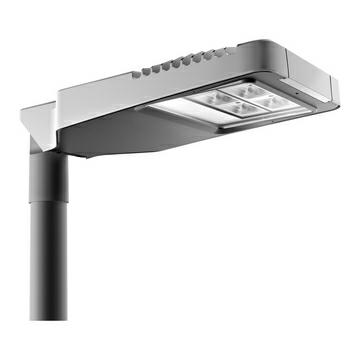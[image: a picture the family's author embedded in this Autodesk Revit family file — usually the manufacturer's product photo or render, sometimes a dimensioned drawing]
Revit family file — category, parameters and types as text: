
# Revit family: Lighting-StreetLighting-GEWISS-ROAD[5]MEDIUM-LED_OPTIC_HUGE_CLI
name_source: partatom
category: Apparecchi per illuminazione
units: mm (PartAtom-declared; Revit-internal decimal feet)

## family parameters
Basato su piano di lavoro = No
Condiviso = No
Punto di calcolo locali = No
Quota connettore circolare = Usa diametro
Sempre verticale = Sì
Sorgente d'illuminazione = No
Taglio con vuoti quando caricato = No
Tipo di parte = Normale

## types (48) — shared parameters
Applicazione = External
Catalogue = LIGHTING
Catalogue Range = ROAD [5]
Electrocod = 244C
IDF = adde9699-6c35-4d07-bf14-12043a13b976
IDT = 9a00d1bcfceb457b92ad59b7f4a86d78
IP degree = IP66
Immagine tipo = GWR5276M.jpg
Insulation class = I
Lamp- = LED
Lampada = LED
Maximum surface exposed to the wind = 0,19M2
Minimum distance from the illuminated object = 1M
Produttore = GEWISS S.p.A.
SEO = Street lighting
Shock resistance = IK08
Technical sheet = https://www.gewiss.com
Tilt adjustable = -20° ÷ +10° side bracket - -10° ÷ +20° pole head
Tipo alimentatore = Constant Current Driver Led
URL = https://www.gewiss.com
Version file RFA = 20.11
Warranty = 5 years

## per-type parameters (varying)
- GWR5616M - ROAD5 MEDI HUGE 6M 4000K 0,85A CL1 1-10V: Colour temperature=4000 K (CRI 70); Colour temperature:=4000 K (CRI 70); Descrizione=ROAD5 MEDI HUGE 6M 4000K 0,85A CL1 1-10V; EAN code=8011564874404; LED LifeTime (L80B05)=120000H; LED current.=0,85A; Lumen output (lm)=17160; Modello=GWR5616M; No. Chorus modules=6 (6x3 LED); Nominal flux (lm)=24330; Number of modules=6 (6x3 LED); Operating temperature:=-25 +40 °C; Optic=H - ULOR: 0%; Overvoltage resistance=12 KV (Common and dfferential mode); Pilot current=0,85A; Power supply operation=Dimmable; System power=185W; Tipologia=Dimmable; Voltage-=220/240 V - 50/60 Hz - Dimmable 1-10 V; Weight (kg)=9.1; Weight (kg):=9,1; Working temperature=-25 +40 °C
- GWR5616B - ROAD5 MEDI HUGE 6M 4000K 0,85A CL1 BIREG: Colour temperature=4000 K (CRI 70); Colour temperature:=4000 K (CRI 70); Descrizione=ROAD5 MED. HUGE 6M 4000K 0,85A CL1 BI-PO; EAN code=8011564874398; LED LifeTime (L80B05)=120000H; LED current.=0,85A; Lumen output (lm)=17160; Modello=GWR5616B; No. Chorus modules=6 (6x3 LED); Nominal flux (lm)=24330; Number of modules=6 (6x3 LED); Operating temperature:=-25 +40 °C; Optic=H - ULOR: 0%; Overvoltage resistance=12 KV (Common and dfferential mode); Pilot current=0,85A; Power supply operation=Bi power; System power=187W; Tipologia=Bi power; Voltage-=220/240 V - 50/60 Hz - Bi-power with self-learning; Weight (kg)=9.1; Weight (kg):=9,1; Working temperature=-25 +40 °C
- GWR5674B30K - ROAD5 MEDI HUGE 4M 3000K 0,7A CL1 BIREG: Body=Die-cast aluminium -; Classification:=-; Color Rendering Index=CRI-70; Colore=Graphite grey; Colour :=Powder coating; Colour temperature=3000K; Colour temperature:=3000 K (CRI>80); Context=Street and parking lighting; Control System=Bi-power with self-learning; DIN 18032-3 certification=-; Descrizione=GWR5674B30K - ROAD5 MEDI HUGE 4M 3000K 0,7A CL1 BIREG; Device with reduced surface temperature=-; Driver=Included; Driver Box=Built-in; Efficiency (lm/W)=96; Eletrical and lighting features=-; External screw=Stainless steel; Fixing=Pole Head - Outreach; Gasket=Anti-aging silicone; General information=-; Glow Wire Test :=-; IPEA=ROAD = A // LARGE AREAS = A ++ // CYCLOPEDONALS = A // GREEN AREAS = A // HISTORICAL CENTER = A3 +; Installationa and maintenance=-; LED Life Time (L80B05)=77000H; LED Maintenance=Not available; LED current.=0,7A; Lifetime=L90B10 (Tq+25°C) = 100.000 h - L90B10 (Tq+50°C) = 50.000 h; Locking Hook=Integrated front handle; Lumen output (lm)=10400; Luminaire=LED Road Equipment; Materials=-; Maximum surface exposed to the wind :=0.19 m2; Modello=GWR5674B30K; Mouting and installation=Pole Head - Outreach; Nominal flux (lm)=10800; Number of modules=4 (4x3 LED); Operating temperature :=-25 +50 °C; Operating temperature:=-25 +50 °C; Optic=HUGE; Optic :=Metallized polycarbonate reflector; Optic Maintenance=Not available; Optic and illuminating features=-; Overvoltage protection=DM 10KV / CM 10KV; Overvoltage resistance :=Common and dfferential mode: 10KV; Photobiological Risk Class=RG0; Power supply operation=Bi power; Rated frequency (Hz)=50 / 60; Shield type=4mm thick flat tempered glass; Standard Deviation Colour Matching=SDCM = 5; Standard-=EN 60598-2-3, EN 60598-1 IEC/TR 62778; Standards and approvals=-; Stocking temperature=-; Supply voltage=220 - 240 V; System power=108W; System power :=108 W @ 0.7A; Tilt-=-20° ÷ +10° side bracket - -10° ÷ +20° pole head; Tipologia=Bi power; Type of light source=LED - Not replaceable; Unified Glare Rating=G*3 - ULOR = 0; Unique digital code (Datamatrix)=Currently not present; Voltage-=220/240 V - 50/60 Hz - Bi-power with self-learning; Weight (kg):=8,4; Wiring=Isolating switch
- GWR561330K - ROAD5 MEDI HUGE 3M 3000K 1,0A CL1: Body=Die-cast aluminium -; Classification:=-; Color Rendering Index=CRI-70; Colore=Graphite grey; Colour :=Powder coating; Colour temperature=3000K; Colour temperature:=3000 K (CRI>80); Context=Street and parking lighting; Control System=Stand alone; DIN 18032-3 certification=-; Descrizione=GWR561330K - ROAD5 MEDI HUGE 3M 3000K 1,0A CL1; Device with reduced surface temperature=-; Driver=Included; Driver Box=Built-in; Efficiency (lm/W)=93; Eletrical and lighting features=-; External screw=Stainless steel; Fixing=Pole Head - Outreach; Gasket=Anti-aging silicone; General information=-; Glow Wire Test :=-; IPEA=ROAD = A // LARGE AREAS = A ++ // CYCLOPEDONALS = B // GREEN AREAS = B // HISTORICAL CENTER = A3 +; Installationa and maintenance=-; LED Life Time (L80B05)=120000H; LED Maintenance=Not available; LED current.=1A; Lifetime=L90B10 (Tq+25°C) = 100.000 h - L90B10 (Tq+40°C) = 75.000 h; Locking Hook=Integrated front handle; Lumen output (lm)=10500; Luminaire=LED Road Equipment; Materials=-; Maximum surface exposed to the wind :=0.19 m2; Modello=GWR561330K; Mouting and installation=Pole Head - Outreach; Nominal flux (lm)=12420; Number of modules=3 (3x3 LED); Operating temperature :=-25 +40 °C; Operating temperature:=-25 +40 °C; Optic=HUGE; Optic :=Metallized polycarbonate reflector; Optic Maintenance=Not available; Optic and illuminating features=-; Overvoltage protection=DM 10KV / CM 10KV; Overvoltage resistance :=Common and dfferential mode: 10KV; Photobiological Risk Class=RG0; Rated frequency (Hz)=50 / 60; Shield type=4mm thick flat tempered glass; Standard Deviation Colour Matching=SDCM = 5; Standard-=EN 60598-2-3, EN 60598-1 IEC/TR 62778; Standards and approvals=-; Stocking temperature=-; Supply voltage=220 - 240 V; System power=113W; System power :=113 W @ 1A; Tilt-=-20° ÷ +10° side bracket - -10° ÷ +20° pole head; Tipologia=Stand alone; Type of light source=LED - Not replaceable; Unified Glare Rating=G*3 - ULOR = 0; Unique digital code (Datamatrix)=Currently not present; Voltage-=220/240 V - 50/60 Hz - Stand alone; Weight (kg):=8; Wiring=Isolating switch
- GWR5616B30K - ROAD5 MEDI HUGE 6M 3000K 0,85A CL1 BIREG: Body=Die-cast aluminium -; Classification:=-; Color Rendering Index=CRI-70; Colore=Graphite grey; Colour :=Powder coating; Colour temperature=3000K; Colour temperature:=3000 K (CRI>80); Context=Street and parking lighting; Control System=Bi-power with self-learning; DIN 18032-3 certification=-; Descrizione=GWR5616B30K - ROAD5 MEDI HUGE 6M 3000K 0,85A CL1 BIREG; Device with reduced surface temperature=-; Driver=Included; Driver Box=Built-in; Efficiency (lm/W)=98; Eletrical and lighting features=-; External screw=Stainless steel; Fixing=Pole Head - Outreach; Gasket=Anti-aging silicone; General information=-; Glow Wire Test :=-; IPEA=ROAD = B // LARGE AREAS = A ++ // CYCLOPEDONALS = B // GREEN AREAS = B // HISTORICAL CENTER = A3 +; Installationa and maintenance=-; LED Life Time (L80B05)=120000H; LED Maintenance=Not available; LED current.=0,849999999999999A; Lifetime=L90B10 (Tq+25°C) = 100.000 h - L90B10 (Tq+40°C) = 50.000 h; Locking Hook=Integrated front handle; Lumen output (lm)=18400; Luminaire=LED Road Equipment; Materials=-; Maximum surface exposed to the wind :=0.19 m2; Modello=GWR5616B30K; Mouting and installation=Pole Head - Outreach; Nominal flux (lm)=21114; Number of modules=6 (6x3 LED); Operating temperature :=-25 +40 °C; Operating temperature:=-25 +40 °C; Optic=HUGE; Optic :=Metallized polycarbonate reflector; Optic Maintenance=Not available; Optic and illuminating features=-; Overvoltage protection=DM 10KV / CM 10KV; Overvoltage resistance :=Common and dfferential mode: 10KV; Photobiological Risk Class=RG0; Power supply operation=Bi power; Rated frequency (Hz)=50 / 60; Shield type=4mm thick flat tempered glass; Standard Deviation Colour Matching=SDCM = 5; Standard-=EN 60598-2-3, EN 60598-1 IEC/TR 62778; Standards and approvals=-; Stocking temperature=-; Supply voltage=220 - 240 V; System power=187W; System power :=187 W @ 0.85A; Tilt-=-20° ÷ +10° side bracket - -10° ÷ +20° pole head; Tipologia=Bi power; Type of light source=LED - Not replaceable; Unified Glare Rating=G*3 - ULOR = 0; Unique digital code (Datamatrix)=Currently not present; Voltage-=220/240 V - 50/60 Hz - Bi-power with self-learning; Weight (kg):=9,09999999999999; Wiring=Isolating switch
- GWR5674M - ROAD5 MEDI HUGE 4M 4000K 0,7A CL1 1-10V: Colour temperature=4000 K (CRI 70); Colour temperature:=4000 K (CRI 70); Descrizione=ROAD5 MEDI HUGE 4M 4000K 0,7A CL1 1-10V; EAN code=8011564874534; LED LifeTime (L80B05)=77000H; LED current.=0,7A; Lumen output (lm)=9190; Modello=GWR5674M; No. Chorus modules=4 (4x3 LED); Nominal flux (lm)=12480; Number of modules=4 (4x3 LED); Operating temperature:=-25 +50 °C; Optic=H - ULOR: 0%; Overvoltage resistance=12 KV (Common and dfferential mode); Pilot current=0,7A; Power supply operation=Dimmable; System power=106W; Tipologia=Dimmable; Voltage-=220/240 V - 50/60 Hz - Dimmable 1-10 V; Weight (kg)=8,4; Weight (kg):=8,4; Working temperature=-25 +50 °C
- GWR5614 - ROAD5 MEDI HUGE 4M 4000K 1,0A CL1: Colour temperature=4000 K (CRI 70); Colour temperature:=4000 K (CRI 70); Descrizione=ROAD5 MEDI HUGE 4M 4000K 1,0A CL1; EAN code=8011564874329; LED LifeTime (L80B05)=120000H; LED current.=1A; Lumen output (lm)=13460; Modello=GWR5614; No. Chorus modules=4 (4x3 LED); Nominal flux (lm)=19080; Number of modules=4 (4x3 LED); Operating temperature:=-25 +40 °C; Optic=H - ULOR: 0%; Overvoltage resistance=12 KV (Common and dfferential mode); Pilot current=1A; System power=151W; Tipologia=Stand alone; Voltage-=220/240 V - 50/60 Hz - Stand alone; Weight (kg)=8,4; Weight (kg):=8,4; Working temperature=-25 +40 °C
- GWR5673M - ROAD5 MEDI HUGE 3M 4000K 0,7A CL1 1-10V: Colour temperature=4000 K (CRI 70); Colour temperature:=4000 K (CRI 70); Descrizione=ROAD5 MEDI HUGE 3M 4000K 0,7A CL1 1-10V; EAN code=8011564874503; LED LifeTime (L80B05)=77000H; LED current.=0,7A; Lumen output (lm)=6890; Modello=GWR5673M; No. Chorus modules=3 (3x3 LED); Nominal flux (lm)=9360; Number of modules=3 (3x3 LED); Operating temperature:=-25 +50 °C; Optic=H - ULOR: 0%; Overvoltage resistance=12 KV (Common and dfferential mode); Pilot current=0,7A; Power supply operation=Dimmable; System power=79W; Tipologia=Dimmable; Voltage-=220/240 V - 50/60 Hz - Dimmable 1-10 V; Weight (kg)=8; Weight (kg):=8; Working temperature=-25 +50 °C
- GWR5676M30K - ROAD5 MEDI HUGE 6M 3000K 0,7A CL1 1-10V: Body=Die-cast aluminium -; Classification:=-; Color Rendering Index=CRI-70; Colore=Graphite grey; Colour :=Powder coating; Colour temperature=3000K; Colour temperature:=3000 K (CRI>80); Context=Street and parking lighting; Control System=Dimmable 1-10 V; DIN 18032-3 certification=-; Descrizione=GWR5676M30K - ROAD5 MEDI HUGE 6M 3000K 0,7A CL1 1-10V; Device with reduced surface temperature=-; Driver=Included; Driver Box=Built-in; Efficiency (lm/W)=97; Eletrical and lighting features=-; External screw=Stainless steel; Fixing=Pole Head - Outreach; Gasket=Anti-aging silicone; General information=-; Glow Wire Test :=-; IPEA=ROAD = B // LARGE AREAS = A ++ // CYCLOPEDONALS = A // GREEN AREAS = A // HISTORICAL CENTER = A3 +; Installationa and maintenance=-; LED Life Time (L80B05)=77000H; LED Maintenance=Not available; LED current.=0,7A; Lifetime=L90B10 (Tq+25°C) = 100.000 h - L90B10 (Tq+50°C) = 50.000 h; Locking Hook=Integrated front handle; Lumen output (lm)=15600; Luminaire=LED Road Equipment; Materials=-; Maximum surface exposed to the wind :=0.19 m2; Modello=GWR5676M30K; Mouting and installation=Pole Head - Outreach; Nominal flux (lm)=16200; Number of modules=6 (6x3 LED); Operating temperature :=-25 +50 °C; Operating temperature:=-25 +50 °C; Optic=HUGE; Optic :=Metallized polycarbonate reflector; Optic Maintenance=Not available; Optic and illuminating features=-; Overvoltage protection=DM 10KV / CM 10KV; Overvoltage resistance :=Common and dfferential mode: 10KV; Photobiological Risk Class=RG0; Power supply operation=Dimmable; Rated frequency (Hz)=50 / 60; Shield type=4mm thick flat tempered glass; Standard Deviation Colour Matching=SDCM = 5; Standard-=EN 60598-2-3, EN 60598-1 IEC/TR 62778; Standards and approvals=-; Stocking temperature=-; Supply voltage=220 - 240 V; System power=159W; System power :=161 W @ 0.7A; Tilt-=-20° ÷ +10° side bracket - -10° ÷ +20° pole head; Tipologia=Dimmable; Type of light source=LED - Not replaceable; Unified Glare Rating=G*3 - ULOR = 0; Unique digital code (Datamatrix)=Currently not present; Voltage-=220/240 V - 50/60 Hz - Dimmable 1-10 V; Weight (kg):=9,09999999999999; Wiring=Isolating switch
- GWR5675 - ROAD5 MEDI HUGE 5M 4000K 0,7A CL1: Colour temperature=4000 K (CRI 70); Colour temperature:=4000 K (CRI 70); Descrizione=ROAD5 MEDI HUGE 5M 4000K 0,7A CL1; EAN code=8011564874541; LED LifeTime (L80B05)=77000H; LED current.=0,7A; Lumen output (lm)=11480; Modello=GWR5675; No. Chorus modules=5 (5x3 LED); Nominal flux (lm)=15600; Number of modules=5 (5x3 LED); Operating temperature:=-25 +50 °C; Optic=H - ULOR: 0%; Overvoltage resistance=12 KV (Common and dfferential mode); Pilot current=0,7A; System power=132W; Tipologia=Stand alone; Voltage-=220/240 V - 50/60 Hz - Stand alone; Weight (kg)=8,8; Weight (kg):=8,8; Working temperature=-25 +50 °C
- GWR5675M - ROAD5 MEDI HUGE 5M 4000K 0,7A CL1 1-10V: Colour temperature=4000 K (CRI 70); Colour temperature:=4000 K (CRI 70); Descrizione=ROAD5 MEDI HUGE 5M 4000K 0,7A CL1 1-10V; EAN code=8011564874565; LED LifeTime (L80B05)=77000H; LED current.=0,7A; Lumen output (lm)=11480; Modello=GWR5675M; No. Chorus modules=5 (5x3 LED); Nominal flux (lm)=15600; Number of modules=5 (5x3 LED); Operating temperature:=-25 +50 °C; Optic=H - ULOR: 0%; Overvoltage resistance=12 KV (Common and dfferential mode); Pilot current=0,7A; Power supply operation=Dimmable; System power=132W; Tipologia=Dimmable; Voltage-=220/240 V - 50/60 Hz - Dimmable 1-10 V; Weight (kg)=8,8; Weight (kg):=8,8; Working temperature=-25 +50 °C
- GWR567430K - ROAD5 MEDI HUGE 4M 3000K 0,7A CL1: Body=Die-cast aluminium -; Classification:=-; Color Rendering Index=CRI-70; Colore=Graphite grey; Colour :=Powder coating; Colour temperature=3000K; Colour temperature:=3000 K (CRI>80); Context=Street and parking lighting; Control System=Stand alone; DIN 18032-3 certification=-; Descrizione=GWR567430K - ROAD5 MEDI HUGE 4M 3000K 0,7A CL1; Device with reduced surface temperature=-; Driver=Included; Driver Box=Built-in; Efficiency (lm/W)=98; Eletrical and lighting features=-; External screw=Stainless steel; Fixing=Pole Head - Outreach; Gasket=Anti-aging silicone; General information=-; Glow Wire Test :=-; IPEA=ROAD = A // LARGE AREAS = A3 + // CYCLOPEDONALS = A // GREEN AREAS = A // HISTORICAL CENTER = A4 +; Installationa and maintenance=-; LED Life Time (L80B05)=77000H; LED Maintenance=Not available; LED current.=0,7A; Lifetime=L90B10 (Tq+25°C) = 100.000 h - L90B10 (Tq+50°C) = 50.000 h; Locking Hook=Integrated front handle; Lumen output (lm)=10400; Luminaire=LED Road Equipment; Materials=-; Maximum surface exposed to the wind :=0.19 m2; Modello=GWR567430K; Mouting and installation=Pole Head - Outreach; Nominal flux (lm)=10800; Number of modules=4 (4x3 LED); Operating temperature :=-25 +50 °C; Operating temperature:=-25 +50 °C; Optic=HUGE; Optic :=Metallized polycarbonate reflector; Optic Maintenance=Not available; Optic and illuminating features=-; Overvoltage protection=DM 10KV / CM 10KV; Overvoltage resistance :=Common and dfferential mode: 10KV; Photobiological Risk Class=RG0; Rated frequency (Hz)=50 / 60; Shield type=4mm thick flat tempered glass; Standard Deviation Colour Matching=SDCM = 5; Standard-=EN 60598-2-3, EN 60598-1 IEC/TR 62778; Standards and approvals=-; Stocking temperature=-; Supply voltage=220 - 240 V; System power=106W; System power :=106 W @ 0.7A; Tilt-=-20° ÷ +10° side bracket - -10° ÷ +20° pole head; Tipologia=Stand alone; Type of light source=LED - Not replaceable; Unified Glare Rating=G*3 - ULOR = 0; Unique digital code (Datamatrix)=Currently not present; Voltage-=220/240 V - 50/60 Hz - Stand alone; Weight (kg):=8,4; Wiring=Isolating switch
- GWR561630K - ROAD5 MEDI HUGE 6M 3000K 0,85A CL1: Body=Die-cast aluminium -; Classification:=-; Color Rendering Index=CRI-70; Colore=Graphite grey; Colour :=Powder coating; Colour temperature=3000K; Colour temperature:=3000 K (CRI>80); Context=Street and parking lighting; Control System=Stand alone; DIN 18032-3 certification=-; Descrizione=GWR561630K - ROAD5 MEDI HUGE 6M 3000K 0,85A CL1; Device with reduced surface temperature=-; Driver=Included; Driver Box=Built-in; Efficiency (lm/W)=99; Eletrical and lighting features=-; External screw=Stainless steel; Fixing=Pole Head - Outreach; Gasket=Anti-aging silicone; General information=-; Glow Wire Test :=-; IPEA=ROAD = B // LARGE AREAS = A ++ // CYCLOPEDONALS = A // GREEN AREAS = A // HISTORICAL CENTER = A3 +; Installationa and maintenance=-; LED Life Time (L80B05)=120000H; LED Maintenance=Not available; LED current.=0,849999999999999A; Lifetime=L90B10 (Tq+25°C) = 100.000 h - L90B10 (Tq+40°C) = 50.000 h; Locking Hook=Integrated front handle; Lumen output (lm)=18400; Luminaire=LED Road Equipment; Materials=-; Maximum surface exposed to the wind :=0.19 m2; Modello=GWR561630K; Mouting and installation=Pole Head - Outreach; Nominal flux (lm)=21114; Number of modules=6 (6x3 LED); Operating temperature :=-25 +40 °C; Operating temperature:=-25 +40 °C; Optic=HUGE; Optic :=Metallized polycarbonate reflector; Optic Maintenance=Not available; Optic and illuminating features=-; Overvoltage protection=DM 10KV / CM 10KV; Overvoltage resistance :=Common and dfferential mode: 10KV; Photobiological Risk Class=RG0; Rated frequency (Hz)=50 / 60; Shield type=4mm thick flat tempered glass; Standard Deviation Colour Matching=SDCM = 5; Standard-=EN 60598-2-3, EN 60598-1 IEC/TR 62778; Standards and approvals=-; Stocking temperature=-; Supply voltage=220 - 240 V; System power=185W; System power :=185 W @ 0.85A; Tilt-=-20° ÷ +10° side bracket - -10° ÷ +20° pole head; Tipologia=Stand alone; Type of light source=LED - Not replaceable; Unified Glare Rating=G*3 - ULOR = 0; Unique digital code (Datamatrix)=Currently not present; Voltage-=220/240 V - 50/60 Hz - Stand alone; Weight (kg):=9,09999999999999; Wiring=Isolating switch
- GWR567630K - ROAD5 MEDI HUGE 6M 3000K 0,7A CL1: Body=Die-cast aluminium -; Classification:=-; Color Rendering Index=CRI-70; Colore=Graphite grey; Colour :=Powder coating; Colour temperature=3000K; Colour temperature:=3000 K (CRI>80); Context=Street and parking lighting; Control System=Stand alone; DIN 18032-3 certification=-; Descrizione=GWR567630K - ROAD5 MEDI HUGE 6M 3000K 0,7A CL1; Device with reduced surface temperature=-; Driver=Included; Driver Box=Built-in; Efficiency (lm/W)=98; Eletrical and lighting features=-; External screw=Stainless steel; Fixing=Pole Head - Outreach; Gasket=Anti-aging silicone; General information=-; Glow Wire Test :=-; IPEA=ROAD = B // LARGE AREAS = A ++ // CYCLOPEDONALS = A // GREEN AREAS = A // HISTORICAL CENTER = A4 +; Installationa and maintenance=-; LED Life Time (L80B05)=77000H; LED Maintenance=Not available; LED current.=0,7A; Lifetime=L90B10 (Tq+25°C) = 100.000 h - L90B10 (Tq+50°C) = 50.000 h; Locking Hook=Integrated front handle; Lumen output (lm)=15600; Luminaire=LED Road Equipment; Materials=-; Maximum surface exposed to the wind :=0.19 m2; Modello=GWR567630K; Mouting and installation=Pole Head - Outreach; Nominal flux (lm)=16200; Number of modules=6 (6x3 LED); Operating temperature :=-25 +50 °C; Operating temperature:=-25 +50 °C; Optic=HUGE; Optic :=Metallized polycarbonate reflector; Optic Maintenance=Not available; Optic and illuminating features=-; Overvoltage protection=DM 10KV / CM 10KV; Overvoltage resistance :=Common and dfferential mode: 10KV; Photobiological Risk Class=RG0; Rated frequency (Hz)=50 / 60; Shield type=4mm thick flat tempered glass; Standard Deviation Colour Matching=SDCM = 5; Standard-=EN 60598-2-3, EN 60598-1 IEC/TR 62778; Standards and approvals=-; Stocking temperature=-; Supply voltage=220 - 240 V; System power=159W; System power :=159 W @ 0.7A; Tilt-=-20° ÷ +10° side bracket - -10° ÷ +20° pole head; Tipologia=Stand alone; Type of light source=LED - Not replaceable; Unified Glare Rating=G*3 - ULOR = 0; Unique digital code (Datamatrix)=Currently not present; Voltage-=220/240 V - 50/60 Hz - Stand alone; Weight (kg):=9,09999999999999; Wiring=Isolating switch
- GWR5676 - ROAD5 MEDI HUGE 6M 4000K 0,7A CL1: Colour temperature=4000 K (CRI 70); Colour temperature:=4000 K (CRI 70); Descrizione=ROAD5 MEDI HUGE 6M 4000K 0,7A CL1; EAN code=8011564874572; LED LifeTime (L80B05)=77000H; LED current.=0,7A; Lumen output (lm)=13780; Modello=GWR5676; No. Chorus modules=6 (6x3 LED); Nominal flux (lm)=18720; Number of modules=6 (6x3 LED); Operating temperature:=-25 +50 °C; Optic=H - ULOR: 0%; Overvoltage resistance=12 KV (Common and dfferential mode); Pilot current=0,7A; System power=159W; Tipologia=Stand alone; Voltage-=220/240 V - 50/60 Hz - Stand alone; Weight (kg)=9.1; Weight (kg):=9,1; Working temperature=-25 +50 °C
- GWR5613 - ROAD5 MEDI HUGE 3M 4000K 1,0A CL1: Colour temperature=4000 K (CRI 70); Colour temperature:=4000 K (CRI 70); Descrizione=ROAD5 MEDI HUGE 3M 4000K 1,0A CL1; EAN code=8011564874091; LED LifeTime (L80B05)=120000H; LED current.=1A; Lumen output (lm)=10100; Modello=GWR5613; No. Chorus modules=3 (3x3 LED); Nominal flux (lm)=14310; Number of modules=3 (3x3 LED); Operating temperature:=-25 +40 °C; Optic=H - ULOR: 0%; Overvoltage resistance=12 KV (Common and dfferential mode); Pilot current=1A; System power=113W; Tipologia=Stand alone; Voltage-=220/240 V - 50/60 Hz - Stand alone; Weight (kg)=8; Weight (kg):=8; Working temperature=-25 +40 °C
- GWR5674M30K - ROAD5 MEDI HUGE 4M 3000K 0,7A CL1 1-10V: Body=Die-cast aluminium -; Classification:=-; Color Rendering Index=CRI-70; Colore=Graphite grey; Colour :=Powder coating; Colour temperature=3000K; Colour temperature:=3000 K (CRI>80); Context=Street and parking lighting; Control System=Dimmable 1-10 V; DIN 18032-3 certification=-; Descrizione=GWR5674M30K - ROAD5 MEDI HUGE 4M 3000K 0,7A CL1 1-10V; Device with reduced surface temperature=-; Driver=Included; Driver Box=Built-in; Efficiency (lm/W)=96; Eletrical and lighting features=-; External screw=Stainless steel; Fixing=Pole Head - Outreach; Gasket=Anti-aging silicone; General information=-; Glow Wire Test :=-; IPEA=ROAD = A // LARGE AREAS = A ++ // CYCLOPEDONALS = A // GREEN AREAS = A // HISTORICAL CENTER = A3 +; Installationa and maintenance=-; LED Life Time (L80B05)=77000H; LED Maintenance=Not available; LED current.=0,7A; Lifetime=L90B10 (Tq+25°C) = 100.000 h - L90B10 (Tq+50°C) = 50.000 h; Locking Hook=Integrated front handle; Lumen output (lm)=10400; Luminaire=LED Road Equipment; Materials=-; Maximum surface exposed to the wind :=0.19 m2; Modello=GWR5674M30K; Mouting and installation=Pole Head - Outreach; Nominal flux (lm)=10800; Number of modules=4 (4x3 LED); Operating temperature :=-25 +50 °C; Operating temperature:=-25 +50 °C; Optic=HUGE; Optic :=Metallized polycarbonate reflector; Optic Maintenance=Not available; Optic and illuminating features=-; Overvoltage protection=DM 10KV / CM 10KV; Overvoltage resistance :=Common and dfferential mode: 10KV; Photobiological Risk Class=RG0; Power supply operation=Dimmable; Rated frequency (Hz)=50 / 60; Shield type=4mm thick flat tempered glass; Standard Deviation Colour Matching=SDCM = 5; Standard-=EN 60598-2-3, EN 60598-1 IEC/TR 62778; Standards and approvals=-; Stocking temperature=-; Supply voltage=220 - 240 V; System power=106W; System power :=108 W @ 0.7A; Tilt-=-20° ÷ +10° side bracket - -10° ÷ +20° pole head; Tipologia=Dimmable; Type of light source=LED - Not replaceable; Unified Glare Rating=G*3 - ULOR = 0; Unique digital code (Datamatrix)=Currently not present; Voltage-=220/240 V - 50/60 Hz - Dimmable 1-10 V; Weight (kg):=8,4; Wiring=Isolating switch
- GWR5673 - ROAD5 MEDI HUGE 3M 4000K 0,7A CL1: Colour temperature=4000 K (CRI 70); Colour temperature:=4000 K (CRI 70); Descrizione=ROAD5 MEDI HUGE 3M 4000K 0,7A CL1; EAN code=8011564874480; LED LifeTime (L80B05)=77000H; LED current.=0,7A; Lumen output (lm)=6890; Modello=GWR5673; No. Chorus modules=3 (3x3 LED); Nominal flux (lm)=9360; Number of modules=3 (3x3 LED); Operating temperature:=-25 +50 °C; Optic=H - ULOR: 0%; Overvoltage resistance=12 KV (Common and dfferential mode); Pilot current=0,7A; System power=79W; Tipologia=Stand alone; Voltage-=220/240 V - 50/60 Hz - Stand alone; Weight (kg)=8; Weight (kg):=8; Working temperature=-25 +50 °C
- GWR5676M - ROAD5 MEDI HUGE 6M 4000K 0,7A CL1 1-10V: Colour temperature=4000 K (CRI 70); Colour temperature:=4000 K (CRI 70); Descrizione=ROAD5 MEDI HUGE 6M 4000K 0,7A CL1 1-10V; EAN code=8011564874596; LED LifeTime (L80B05)=77000H; LED current.=0,7A; Lumen output (lm)=13780; Modello=GWR5676M; No. Chorus modules=6 (6x3 LED); Nominal flux (lm)=18720; Number of modules=6 (6x3 LED); Operating temperature:=-25 +50 °C; Optic=H - ULOR: 0%; Overvoltage resistance=12 KV (Common and dfferential mode); Pilot current=0,7A; Power supply operation=Dimmable; System power=159W; Tipologia=Dimmable; Voltage-=220/240 V - 50/60 Hz - Dimmable 1-10 V; Weight (kg)=9.1; Weight (kg):=9,1; Working temperature=-25 +50 °C
- GWR5676B - ROAD5 MEDI HUGE 6M 4000K 0,7A CL1 BIREG: Colour temperature=4000 K (CRI 70); Colour temperature:=4000 K (CRI 70); Descrizione=ROAD5 MED. HUGE 6M 4000K 0,7A CL1 BI-PO.; EAN code=8011564874589; LED LifeTime (L80B05)=77000H; LED current.=0,7A; Lumen output (lm)=13780; Modello=GWR5676B; No. Chorus modules=6 (6x3 LED); Nominal flux (lm)=18720; Number of modules=6 (6x3 LED); Operating temperature:=-25 +50 °C; Optic=H - ULOR: 0%; Overvoltage resistance=12 KV (Common and dfferential mode); Pilot current=0,7A; Power supply operation=Bi power; System power=161W; Tipologia=Bi power; Voltage-=220/240 V - 50/60 Hz - Bi-power with self-learning; Weight (kg)=9.1; Weight (kg):=9,1; Working temperature=-25 +50 °C
- GWR5613M - ROAD5 MEDI HUGE 3M 4000K 1,0A CL1 1-10V: Colour temperature=4000 K (CRI 70); Colour temperature:=4000 K (CRI 70); Descrizione=ROAD5 MEDI HUGE 3M 4000K 1,0A CL1 1-10V; EAN code=8011564874312; LED LifeTime (L80B05)=120000H; LED current.=1A; Lumen output (lm)=10100; Modello=GWR5613M; No. Chorus modules=3 (3x3 LED); Nominal flux (lm)=14310; Number of modules=3 (3x3 LED); Operating temperature:=-25 +40 °C; Optic=H - ULOR: 0%; Overvoltage resistance=12 KV (Common and dfferential mode); Pilot current=1A; Power supply operation=Dimmable; System power=113W; Tipologia=Dimmable; Voltage-=220/240 V - 50/60 Hz - Dimmable 1-10 V; Weight (kg)=8; Weight (kg):=8; Working temperature=-25 +40 °C
- GWR5676B30K - ROAD5 MEDI HUGE 6M 3000K 0,7A CL1 BIREG: Body=Die-cast aluminium -; Classification:=-; Color Rendering Index=CRI-70; Colore=Graphite grey; Colour :=Powder coating; Colour temperature=3000K; Colour temperature:=3000 K (CRI>80); Context=Street and parking lighting; Control System=Bi-power with self-learning; DIN 18032-3 certification=-; Descrizione=GWR5676B30K - ROAD5 MEDI HUGE 6M 3000K 0,7A CL1 BIREG; Device with reduced surface temperature=-; Driver=Included; Driver Box=Built-in; Efficiency (lm/W)=97; Eletrical and lighting features=-; External screw=Stainless steel; Fixing=Pole Head - Outreach; Gasket=Anti-aging silicone; General information=-; Glow Wire Test :=-; IPEA=ROAD = B // LARGE AREAS = A ++ // CYCLOPEDONALS = A // GREEN AREAS = A // HISTORICAL CENTER = A3 +; Installationa and maintenance=-; LED Life Time (L80B05)=77000H; LED Maintenance=Not available; LED current.=0,7A; Lifetime=L90B10 (Tq+25°C) = 100.000 h - L90B10 (Tq+50°C) = 50.000 h; Locking Hook=Integrated front handle; Lumen output (lm)=15600; Luminaire=LED Road Equipment; Materials=-; Maximum surface exposed to the wind :=0.19 m2; Modello=GWR5676B30K; Mouting and installation=Pole Head - Outreach; Nominal flux (lm)=16200; Number of modules=6 (6x3 LED); Operating temperature :=-25 +50 °C; Operating temperature:=-25 +50 °C; Optic=HUGE; Optic :=Metallized polycarbonate reflector; Optic Maintenance=Not available; Optic and illuminating features=-; Overvoltage protection=DM 10KV / CM 10KV; Overvoltage resistance :=Common and dfferential mode: 10KV; Photobiological Risk Class=RG0; Power supply operation=Bi power; Rated frequency (Hz)=50 / 60; Shield type=4mm thick flat tempered glass; Standard Deviation Colour Matching=SDCM = 5; Standard-=EN 60598-2-3, EN 60598-1 IEC/TR 62778; Standards and approvals=-; Stocking temperature=-; Supply voltage=220 - 240 V; System power=161W; System power :=161 W @ 0.7A; Tilt-=-20° ÷ +10° side bracket - -10° ÷ +20° pole head; Tipologia=Bi power; Type of light source=LED - Not replaceable; Unified Glare Rating=G*3 - ULOR = 0; Unique digital code (Datamatrix)=Currently not present; Voltage-=220/240 V - 50/60 Hz - Bi-power with self-learning; Weight (kg):=9,09999999999999; Wiring=Isolating switch
- GWR5615M30K - ROAD5 MEDI HUGE 5M 3000K 0,85A CL1 1-10V: Body=Die-cast aluminium -; Classification:=-; Color Rendering Index=CRI-70; Colore=Graphite grey; Colour :=Powder coating; Colour temperature=3000K; Colour temperature:=3000 K (CRI>80); Context=Street and parking lighting; Control System=Dimmable 1-10 V; DIN 18032-3 certification=-; Descrizione=GWR5615M30K - ROAD5 MEDI HUGE 5M 3000K 0,85A CL1 1-10V; Device with reduced surface temperature=-; Driver=Included; Driver Box=Built-in; Efficiency (lm/W)=95; Eletrical and lighting features=-; External screw=Stainless steel; Fixing=Pole Head - Outreach; Gasket=Anti-aging silicone; General information=-; Glow Wire Test :=-; IPEA=ROAD = B // LARGE AREAS = A ++ // CYCLOPEDONALS = B // GREEN AREAS = B // HISTORICAL CENTER = A3 +; Installationa and maintenance=-; LED Life Time (L80B05)=120000H; LED Maintenance=Not available; LED current.=0,849999999999999A; Lifetime=L90B10 (Tq+25°C) = 100.000 h - L90B10 (Tq+40°C) = 50.000 h; Locking Hook=Integrated front handle; Lumen output (lm)=15300; Luminaire=LED Road Equipment; Materials=-; Maximum surface exposed to the wind :=0.19 m2; Modello=GWR5615M30K; Mouting and installation=Pole Head - Outreach; Nominal flux (lm)=18423; Number of modules=5 (5x3 LED); Operating temperature :=-25 +40 °C; Operating temperature:=-25 +40 °C; Optic=HUGE; Optic :=Metallized polycarbonate reflector; Optic Maintenance=Not available; Optic and illuminating features=-; Overvoltage protection=DM 10KV / CM 10KV; Overvoltage resistance :=Common and dfferential mode: 10KV; Photobiological Risk Class=RG0; Power supply operation=Dimmable; Rated frequency (Hz)=50 / 60; Shield type=4mm thick flat tempered glass; Standard Deviation Colour Matching=SDCM = 5; Standard-=EN 60598-2-3, EN 60598-1 IEC/TR 62778; Standards and approvals=-; Stocking temperature=-; Supply voltage=220 - 240 V; System power=159W; System power :=161 W @ 0.85A; Tilt-=-20° ÷ +10° side bracket - -10° ÷ +20° pole head; Tipologia=Dimmable; Type of light source=LED - Not replaceable; Unified Glare Rating=G*3 - ULOR = 0; Unique digital code (Datamatrix)=Currently not present; Voltage-=220/240 V - 50/60 Hz - Dimmable 1-10 V; Weight (kg):=8,8; Wiring=Isolating switch
- GWR567330K - ROAD5 MEDI HUGE 3M 3000K 0,7A CL1: Body=Die-cast aluminium -; Classification:=-; Color Rendering Index=CRI-70; Colore=Graphite grey; Colour :=Powder coating; Colour temperature=3000K; Colour temperature:=3000 K (CRI>80); Context=Street and parking lighting; Control System=Stand alone; DIN 18032-3 certification=-; Descrizione=GWR567330K - ROAD5 MEDI HUGE 3M 3000K 0,7A CL1; Device with reduced surface temperature=-; Driver=Included; Driver Box=Built-in; Efficiency (lm/W)=99; Eletrical and lighting features=-; External screw=Stainless steel; Fixing=Pole Head - Outreach; Gasket=Anti-aging silicone; General information=-; Glow Wire Test :=-; IPEA=ROAD = A ++ // LARGE AREAS = A3 + // CYCLOPEDONALS = A + // GREEN AREAS = A + // HISTORICAL CENTER = A5 +; Installationa and maintenance=-; LED Life Time (L80B05)=77000H; LED Maintenance=Not available; LED current.=0,7A; Lifetime=L90B10 (Tq+25°C) = 100.000 h - L90B10 (Tq+50°C) = 75.000 h; Locking Hook=Integrated front handle; Lumen output (lm)=7800; Luminaire=LED Road Equipment; Materials=-; Maximum surface exposed to the wind :=0.19 m2; Modello=GWR567330K; Mouting and installation=Pole Head - Outreach; Nominal flux (lm)=8100; Number of modules=3 (3x3 LED); Operating temperature :=-25 +50 °C; Operating temperature:=-25 +50 °C; Optic=HUGE; Optic :=Metallized polycarbonate reflector; Optic Maintenance=Not available; Optic and illuminating features=-; Overvoltage protection=DM 10KV / CM 10KV; Overvoltage resistance :=Common and dfferential mode: 10KV; Photobiological Risk Class=RG0; Rated frequency (Hz)=50 / 60; Shield type=4mm thick flat tempered glass; Standard Deviation Colour Matching=SDCM = 5; Standard-=EN 60598-2-3, EN 60598-1 IEC/TR 62778; Standards and approvals=-; Stocking temperature=-; Supply voltage=220 - 240 V; System power=79W; System power :=79 W @ 0.7A; Tilt-=-20° ÷ +10° side bracket - -10° ÷ +20° pole head; Tipologia=Stand alone; Type of light source=LED - Not replaceable; Unified Glare Rating=G*3 - ULOR = 0; Unique digital code (Datamatrix)=Currently not present; Voltage-=220/240 V - 50/60 Hz - Stand alone; Weight (kg):=8; Wiring=Isolating switch
- GWR5674B - ROAD5 MEDI HUGE 4M 4000K 0,7A CL1 BIREG: Colour temperature=4000 K (CRI 70); Colour temperature:=4000 K (CRI 70); Descrizione=ROAD5 MEDI HUGE 4M 4000K 0,7A CL1 BI-POW; EAN code=8011564874527; LED LifeTime (L80B05)=77000H; LED current.=0,7A; Lumen output (lm)=9190; Modello=GWR5674B; No. Chorus modules=4 (4x3 LED); Nominal flux (lm)=12480; Number of modules=4 (4x3 LED); Operating temperature:=-25 +50 °C; Optic=H - ULOR: 0%; Overvoltage resistance=12 KV (Common and dfferential mode); Pilot current=0,7A; Power supply operation=Bi power; System power=108W; Tipologia=Bi power; Voltage-=220/240 V - 50/60 Hz - Bi-power with self-learning; Weight (kg)=8,4; Weight (kg):=8,4; Working temperature=-25 +50 °C
- GWR5613B30K - ROAD5 MEDI HUGE 3M 3000K 1,0A CL1 BIREG: Body=Die-cast aluminium -; Classification:=-; Color Rendering Index=CRI-70; Colore=Graphite grey; Colour :=Powder coating; Colour temperature=3000K; Colour temperature:=3000 K (CRI>80); Context=Street and parking lighting; Control System=Bi-power with self-learning; DIN 18032-3 certification=-; Descrizione=GWR5613B30K - ROAD5 MEDI HUGE 3M 3000K 1,0A CL1 BIREG; Device with reduced surface temperature=-; Driver=Included; Driver Box=Built-in; Efficiency (lm/W)=91; Eletrical and lighting features=-; External screw=Stainless steel; Fixing=Pole Head - Outreach; Gasket=Anti-aging silicone; General information=-; Glow Wire Test :=-; IPEA=ROAD = A // LARGE AREAS = A ++ // CYCLOPEDONALS = B // GREEN AREAS = B // HISTORICAL CENTER = A3 +; Installationa and maintenance=-; LED Life Time (L80B05)=120000H; LED Maintenance=Not available; LED current.=1A; Lifetime=L90B10 (Tq+25°C) = 100.000 h - L90B10 (Tq+40°C) = 75.000 h; Locking Hook=Integrated front handle; Lumen output (lm)=10500; Luminaire=LED Road Equipment; Materials=-; Maximum surface exposed to the wind :=0.19 m2; Modello=GWR5613B30K; Mouting and installation=Pole Head - Outreach; Nominal flux (lm)=12420; Number of modules=3 (3x3 LED); Operating temperature :=-25 +40 °C; Operating temperature:=-25 +40 °C; Optic=HUGE; Optic :=Metallized polycarbonate reflector; Optic Maintenance=Not available; Optic and illuminating features=-; Overvoltage protection=DM 10KV / CM 10KV; Overvoltage resistance :=Common and dfferential mode: 10KV; Photobiological Risk Class=RG0; Power supply operation=Bi power; Rated frequency (Hz)=50 / 60; Shield type=4mm thick flat tempered glass; Standard Deviation Colour Matching=SDCM = 5; Standard-=EN 60598-2-3, EN 60598-1 IEC/TR 62778; Standards and approvals=-; Stocking temperature=-; Supply voltage=220 - 240 V; System power=115W; System power :=115 W @ 1A; Tilt-=-20° ÷ +10° side bracket - -10° ÷ +20° pole head; Tipologia=Bi power; Type of light source=LED - Not replaceable; Unified Glare Rating=G*3 - ULOR = 0; Unique digital code (Datamatrix)=Currently not present; Voltage-=220/240 V - 50/60 Hz - Bi-power with self-learning; Weight (kg):=8; Wiring=Isolating switch
- GWR5674 - ROAD5 MEDI HUGE 4M 4000K 0,7A CL1: Colour temperature=4000 K (CRI 70); Colour temperature:=4000 K (CRI 70); Descrizione=ROAD5 MEDI HUGE 4M 4000K 0,7A CL1; EAN code=8011564874510; LED LifeTime (L80B05)=77000H; LED current.=0,7A; Lumen output (lm)=9190; Modello=GWR5674; No. Chorus modules=4 (4x3 LED); Nominal flux (lm)=12480; Number of modules=4 (4x3 LED); Operating temperature:=-25 +50 °C; Optic=H - ULOR: 0%; Overvoltage resistance=12 KV (Common and dfferential mode); Pilot current=0,7A; System power=106W; Tipologia=Stand alone; Voltage-=220/240 V - 50/60 Hz - Stand alone; Weight (kg)=8,4; Weight (kg):=8,4; Working temperature=-25 +50 °C
- GWR5613B - ROAD5 MEDI HUGE 3M 4000K 1,0A CL1 BIREG: Colour temperature=4000 K (CRI 70); Colour temperature:=4000 K (CRI 70); Descrizione=ROAD5 MEDI HUGE 3M 4000K 1,0A CL1 BI-POW; EAN code=8011564874107; LED LifeTime (L80B05)=120000H; LED current.=1A; Lumen output (lm)=10100; Modello=GWR5613B; No. Chorus modules=3 (3x3 LED); Nominal flux (lm)=14310; Number of modules=3 (3x3 LED); Operating temperature:=-25 +40 °C; Optic=H - ULOR: 0%; Overvoltage resistance=12 KV (Common and dfferential mode); Pilot current=1A; Power supply operation=Bi power; System power=115W; Tipologia=Bi power; Voltage-=220/240 V - 50/60 Hz - Bi-power with self-learning; Weight (kg)=8; Weight (kg):=8; Working temperature=-25 +40 °C
- GWR567530K - ROAD5 MEDI HUGE 5M 3000K 0,7A CL1: Body=Die-cast aluminium -; Classification:=-; Color Rendering Index=CRI-70; Colore=Graphite grey; Colour :=Powder coating; Colour temperature=3000K; Colour temperature:=3000 K (CRI>80); Context=Street and parking lighting; Control System=Stand alone; DIN 18032-3 certification=-; Descrizione=GWR567530K - ROAD5 MEDI HUGE 5M 3000K 0,7A CL1; Device with reduced surface temperature=-; Driver=Included; Driver Box=Built-in; Efficiency (lm/W)=98; Eletrical and lighting features=-; External screw=Stainless steel; Fixing=Pole Head - Outreach; Gasket=Anti-aging silicone; General information=-; Glow Wire Test :=-; IPEA=ROAD = B // LARGE AREAS = A ++ // CYCLOPEDONALS = A // GREEN AREAS = A // HISTORICAL CENTER = A4 +; Installationa and maintenance=-; LED Life Time (L80B05)=77000H; LED Maintenance=Not available; LED current.=0,7A; Lifetime=L90B10 (Tq+25°C) = 100.000 h - L90B10 (Tq+50°C) = 50.000 h; Locking Hook=Integrated front handle; Lumen output (lm)=13000; Luminaire=LED Road Equipment; Materials=-; Maximum surface exposed to the wind :=0.19 m2; Modello=GWR567530K; Mouting and installation=Pole Head - Outreach; Nominal flux (lm)=13500; Number of modules=5 (5x3 LED); Operating temperature :=-25 +50 °C; Operating temperature:=-25 +50 °C; Optic=HUGE; Optic :=Metallized polycarbonate reflector; Optic Maintenance=Not available; Optic and illuminating features=-; Overvoltage protection=DM 10KV / CM 10KV; Overvoltage resistance :=Common and dfferential mode: 10KV; Photobiological Risk Class=RG0; Rated frequency (Hz)=50 / 60; Shield type=4mm thick flat tempered glass; Standard Deviation Colour Matching=SDCM = 5; Standard-=EN 60598-2-3, EN 60598-1 IEC/TR 62778; Standards and approvals=-; Stocking temperature=-; Supply voltage=220 - 240 V; System power=132W; System power :=132 W @ 0.7A; Tilt-=-20° ÷ +10° side bracket - -10° ÷ +20° pole head; Tipologia=Stand alone; Type of light source=LED - Not replaceable; Unified Glare Rating=G*3 - ULOR = 0; Unique digital code (Datamatrix)=Currently not present; Voltage-=220/240 V - 50/60 Hz - Stand alone; Weight (kg):=8,8; Wiring=Isolating switch
- GWR5673B30K - ROAD5 MEDI HUGE 3M 3000K 0,7A CL1 BIREG: Body=Die-cast aluminium -; Classification:=-; Color Rendering Index=CRI-70; Colore=Graphite grey; Colour :=Powder coating; Colour temperature=3000K; Colour temperature:=3000 K (CRI>80); Context=Street and parking lighting; Control System=Bi-power with self-learning; DIN 18032-3 certification=-; Descrizione=GWR5673B30K - ROAD5 MEDI HUGE 3M 3000K 0,7A CL1 BIREG; Device with reduced surface temperature=-; Driver=Included; Driver Box=Built-in; Efficiency (lm/W)=96; Eletrical and lighting features=-; External screw=Stainless steel; Fixing=Pole Head - Outreach; Gasket=Anti-aging silicone; General information=-; Glow Wire Test :=-; IPEA=ROAD = A + // LARGE AREAS = A ++ // CYCLOPEDONALS = A + // GREEN AREAS = A + // HISTORICAL CENTER = A5 +; Installationa and maintenance=-; LED Life Time (L80B05)=77000H; LED Maintenance=Not available; LED current.=0,7A; Lifetime=L90B10 (Tq+25°C) = 100.000 h - L90B10 (Tq+50°C) = 75.000 h; Locking Hook=Integrated front handle; Lumen output (lm)=7800; Luminaire=LED Road Equipment; Materials=-; Maximum surface exposed to the wind :=0.19 m2; Modello=GWR5673B30K; Mouting and installation=Pole Head - Outreach; Nominal flux (lm)=8100; Number of modules=3 (3x3 LED); Operating temperature :=-25 +50 °C; Operating temperature:=-25 +50 °C; Optic=HUGE; Optic :=Metallized polycarbonate reflector; Optic Maintenance=Not available; Optic and illuminating features=-; Overvoltage protection=DM 10KV / CM 10KV; Overvoltage resistance :=Common and dfferential mode: 10KV; Photobiological Risk Class=RG0; Power supply operation=Bi power; Rated frequency (Hz)=50 / 60; Shield type=4mm thick flat tempered glass; Standard Deviation Colour Matching=SDCM = 5; Standard-=EN 60598-2-3, EN 60598-1 IEC/TR 62778; Standards and approvals=-; Stocking temperature=-; Supply voltage=220 - 240 V; System power=81W; System power :=81 W @ 0.7A; Tilt-=-20° ÷ +10° side bracket - -10° ÷ +20° pole head; Tipologia=Bi power; Type of light source=LED - Not replaceable; Unified Glare Rating=G*3 - ULOR = 0; Unique digital code (Datamatrix)=Currently not present; Voltage-=220/240 V - 50/60 Hz - Bi-power with self-learning; Weight (kg):=8; Wiring=Isolating switch
- GWR5675B30K - ROAD5 MEDI HUGE 5M 3000K 0,7A CL1 BIREG: Body=Die-cast aluminium -; Classification:=-; Color Rendering Index=CRI-70; Colore=Graphite grey; Colour :=Powder coating; Colour temperature=3000K; Colour temperature:=3000 K (CRI>80); Context=Street and parking lighting; Control System=Bi-power with self-learning; DIN 18032-3 certification=-; Descrizione=GWR5675B30K - ROAD5 MEDI HUGE 5M 3000K 0,7A CL1 BIREG; Device with reduced surface temperature=-; Driver=Included; Driver Box=Built-in; Efficiency (lm/W)=97; Eletrical and lighting features=-; External screw=Stainless steel; Fixing=Pole Head - Outreach; Gasket=Anti-aging silicone; General information=-; Glow Wire Test :=-; IPEA=ROAD = B // LARGE AREAS = A ++ // CYCLOPEDONALS = A // GREEN AREAS = A // HISTORICAL CENTER = A3 +; Installationa and maintenance=-; LED Life Time (L80B05)=77000H; LED Maintenance=Not available; LED current.=0,7A; Lifetime=L90B10 (Tq+25°C) = 100.000 h - L90B10 (Tq+50°C) = 50.000 h; Locking Hook=Integrated front handle; Lumen output (lm)=13000; Luminaire=LED Road Equipment; Materials=-; Maximum surface exposed to the wind :=0.19 m2; Modello=GWR5675B30K; Mouting and installation=Pole Head - Outreach; Nominal flux (lm)=13500; Number of modules=5 (5x3 LED); Operating temperature :=-25 +50 °C; Operating temperature:=-25 +50 °C; Optic=HUGE; Optic :=Metallized polycarbonate reflector; Optic Maintenance=Not available; Optic and illuminating features=-; Overvoltage protection=DM 10KV / CM 10KV; Overvoltage resistance :=Common and dfferential mode: 10KV; Photobiological Risk Class=RG0; Power supply operation=Bi power; Rated frequency (Hz)=50 / 60; Shield type=4mm thick flat tempered glass; Standard Deviation Colour Matching=SDCM = 5; Standard-=EN 60598-2-3, EN 60598-1 IEC/TR 62778; Standards and approvals=-; Stocking temperature=-; Supply voltage=220 - 240 V; System power=134W; System power :=134 W @ 0.7A; Tilt-=-20° ÷ +10° side bracket - -10° ÷ +20° pole head; Tipologia=Bi power; Type of light source=LED - Not replaceable; Unified Glare Rating=G*3 - ULOR = 0; Unique digital code (Datamatrix)=Currently not present; Voltage-=220/240 V - 50/60 Hz - Bi-power with self-learning; Weight (kg):=8,8; Wiring=Isolating switch
- GWR5673M30K - ROAD5 MEDI HUGE 3M 3000K 0,7A CL1 1-10V: Body=Die-cast aluminium -; Classification:=-; Color Rendering Index=CRI-70; Colore=Graphite grey; Colour :=Powder coating; Colour temperature=3000K; Colour temperature:=3000 K (CRI>80); Context=Street and parking lighting; Control System=Dimmable 1-10 V; DIN 18032-3 certification=-; Descrizione=GWR5673M30K - ROAD5 MEDI HUGE 3M 3000K 0,7A CL1 1-10V; Device with reduced surface temperature=-; Driver=Included; Driver Box=Built-in; Efficiency (lm/W)=96; Eletrical and lighting features=-; External screw=Stainless steel; Fixing=Pole Head - Outreach; Gasket=Anti-aging silicone; General information=-; Glow Wire Test :=-; IPEA=ROAD = A + // LARGE AREAS = A ++ // CYCLOPEDONALS = A + // GREEN AREAS = A + // HISTORICAL CENTER = A5 +; Installationa and maintenance=-; LED Life Time (L80B05)=77000H; LED Maintenance=Not available; LED current.=0,7A; Lifetime=L90B10 (Tq+25°C) = 100.000 h - L90B10 (Tq+50°C) = 75.000 h; Locking Hook=Integrated front handle; Lumen output (lm)=7800; Luminaire=LED Road Equipment; Materials=-; Maximum surface exposed to the wind :=0.19 m2; Modello=GWR5673M30K; Mouting and installation=Pole Head - Outreach; Nominal flux (lm)=8100; Number of modules=3 (3x3 LED); Operating temperature :=-25 +50 °C; Operating temperature:=-25 +50 °C; Optic=HUGE; Optic :=Metallized polycarbonate reflector; Optic Maintenance=Not available; Optic and illuminating features=-; Overvoltage protection=DM 10KV / CM 10KV; Overvoltage resistance :=Common and dfferential mode: 10KV; Photobiological Risk Class=RG0; Power supply operation=Dimmable; Rated frequency (Hz)=50 / 60; Shield type=4mm thick flat tempered glass; Standard Deviation Colour Matching=SDCM = 5; Standard-=EN 60598-2-3, EN 60598-1 IEC/TR 62778; Standards and approvals=-; Stocking temperature=-; Supply voltage=220 - 240 V; System power=79W; System power :=81 W @ 0.7A; Tilt-=-20° ÷ +10° side bracket - -10° ÷ +20° pole head; Tipologia=Dimmable; Type of light source=LED - Not replaceable; Unified Glare Rating=G*3 - ULOR = 0; Unique digital code (Datamatrix)=Currently not present; Voltage-=220/240 V - 50/60 Hz - Dimmable 1-10 V; Weight (kg):=8; Wiring=Isolating switch
- GWR5615B30K - ROAD5 MEDI HUGE 5M 3000K 0,85A CL1 BIREG: Body=Die-cast aluminium -; Classification:=-; Color Rendering Index=CRI-70; Colore=Graphite grey; Colour :=Powder coating; Colour temperature=3000K; Colour temperature:=3000 K (CRI>80); Context=Street and parking lighting; Control System=Bi-power with self-learning; DIN 18032-3 certification=-; Descrizione=GWR5615B30K - ROAD5 MEDI HUGE 5M 3000K 0,85A CL1 BIREG; Device with reduced surface temperature=-; Driver=Included; Driver Box=Built-in; Efficiency (lm/W)=95; Eletrical and lighting features=-; External screw=Stainless steel; Fixing=Pole Head - Outreach; Gasket=Anti-aging silicone; General information=-; Glow Wire Test :=-; IPEA=ROAD = B // LARGE AREAS = A ++ // CYCLOPEDONALS = B // GREEN AREAS = B // HISTORICAL CENTER = A3 +; Installationa and maintenance=-; LED Life Time (L80B05)=120000H; LED Maintenance=Not available; LED current.=0,849999999999999A; Lifetime=L90B10 (Tq+25°C) = 100.000 h - L90B10 (Tq+40°C) = 50.000 h; Locking Hook=Integrated front handle; Lumen output (lm)=15300; Luminaire=LED Road Equipment; Materials=-; Maximum surface exposed to the wind :=0.19 m2; Modello=GWR5615B30K; Mouting and installation=Pole Head - Outreach; Nominal flux (lm)=18423; Number of modules=5 (5x3 LED); Operating temperature :=-25 +40 °C; Operating temperature:=-25 +40 °C; Optic=HUGE; Optic :=Metallized polycarbonate reflector; Optic Maintenance=Not available; Optic and illuminating features=-; Overvoltage protection=DM 10KV / CM 10KV; Overvoltage resistance :=Common and dfferential mode: 10KV; Photobiological Risk Class=RG0; Power supply operation=Bi power; Rated frequency (Hz)=50 / 60; Shield type=4mm thick flat tempered glass; Standard Deviation Colour Matching=SDCM = 5; Standard-=EN 60598-2-3, EN 60598-1 IEC/TR 62778; Standards and approvals=-; Stocking temperature=-; Supply voltage=220 - 240 V; System power=161W; System power :=161 W @ 0.85A; Tilt-=-20° ÷ +10° side bracket - -10° ÷ +20° pole head; Tipologia=Bi power; Type of light source=LED - Not replaceable; Unified Glare Rating=G*3 - ULOR = 0; Unique digital code (Datamatrix)=Currently not present; Voltage-=220/240 V - 50/60 Hz - Bi-power with self-learning; Weight (kg):=8,8; Wiring=Isolating switch
- GWR5616M30K - ROAD5 MEDI HUGE 6M 3000K 0,85A CL1 1-10V: Body=Die-cast aluminium -; Classification:=-; Color Rendering Index=CRI-70; Colore=Graphite grey; Colour :=Powder coating; Colour temperature=3000K; Colour temperature:=3000 K (CRI>80); Context=Street and parking lighting; Control System=Dimmable 1-10 V; DIN 18032-3 certification=-; Descrizione=GWR5616M30K - ROAD5 MEDI HUGE 6M 3000K 0,85A CL1 1-10V; Device with reduced surface temperature=-; Driver=Included; Driver Box=Built-in; Efficiency (lm/W)=98; Eletrical and lighting features=-; External screw=Stainless steel; Fixing=Pole Head - Outreach; Gasket=Anti-aging silicone; General information=-; Glow Wire Test :=-; IPEA=ROAD = B // LARGE AREAS = A ++ // CYCLOPEDONALS = B // GREEN AREAS = B // HISTORICAL CENTER = A3 +; Installationa and maintenance=-; LED Life Time (L80B05)=120000H; LED Maintenance=Not available; LED current.=0,849999999999999A; Lifetime=L90B10 (Tq+25°C) = 100.000 h - L90B10 (Tq+40°C) = 50.000 h; Locking Hook=Integrated front handle; Lumen output (lm)=18400; Luminaire=LED Road Equipment; Materials=-; Maximum surface exposed to the wind :=0.19 m2; Modello=GWR5616M30K; Mouting and installation=Pole Head - Outreach; Nominal flux (lm)=21114; Number of modules=6 (6x3 LED); Operating temperature :=-25 +40 °C; Operating temperature:=-25 +40 °C; Optic=HUGE; Optic :=Metallized polycarbonate reflector; Optic Maintenance=Not available; Optic and illuminating features=-; Overvoltage protection=DM 10KV / CM 10KV; Overvoltage resistance :=Common and dfferential mode: 10KV; Photobiological Risk Class=RG0; Power supply operation=Dimmable; Rated frequency (Hz)=50 / 60; Shield type=4mm thick flat tempered glass; Standard Deviation Colour Matching=SDCM = 5; Standard-=EN 60598-2-3, EN 60598-1 IEC/TR 62778; Standards and approvals=-; Stocking temperature=-; Supply voltage=220 - 240 V; System power=185W; System power :=187 W @ 0.85A; Tilt-=-20° ÷ +10° side bracket - -10° ÷ +20° pole head; Tipologia=Dimmable; Type of light source=LED - Not replaceable; Unified Glare Rating=G*3 - ULOR = 0; Unique digital code (Datamatrix)=Currently not present; Voltage-=220/240 V - 50/60 Hz - Dimmable 1-10 V; Weight (kg):=9,09999999999999; Wiring=Isolating switch
- GWR5673B - ROAD5 MEDI HUGE 3M 4000K 0,7A CL1 BIREG: Colour temperature=4000 K (CRI 70); Colour temperature:=4000 K (CRI 70); Descrizione=ROAD5 MEDI HUGE 3M 4000K 0,7A CL1 BI-POW; EAN code=8011564874497; LED LifeTime (L80B05)=77000H; LED current.=0,7A; Lumen output (lm)=6890; Modello=GWR5673B; No. Chorus modules=3 (3x3 LED); Nominal flux (lm)=9360; Number of modules=3 (3x3 LED); Operating temperature:=-25 +50 °C; Optic=H - ULOR: 0%; Overvoltage resistance=12 KV (Common and dfferential mode); Pilot current=0,7A; Power supply operation=Bi power; System power=81W; Tipologia=Bi power; Voltage-=220/240 V - 50/60 Hz - Bi-power with self-learning; Weight (kg)=8; Weight (kg):=8; Working temperature=-25 +50 °C
- GWR5614B - ROAD5 MEDI HUGE 4M 4000K 1,0A CL1 BIREG: Colour temperature=4000 K (CRI 70); Colour temperature:=4000 K (CRI 70); Descrizione=ROAD5 MEDI HUGE 4M 4000K 1,0A CL1 BI-POW; EAN code=8011564874336; LED LifeTime (L80B05)=120000H; LED current.=1A; Lumen output (lm)=13460; Modello=GWR5614B; No. Chorus modules=4 (4x3 LED); Nominal flux (lm)=19080; Number of modules=4 (4x3 LED); Operating temperature:=-25 +40 °C; Optic=H - ULOR: 0%; Overvoltage resistance=12 KV (Common and dfferential mode); Pilot current=1A; Power supply operation=Bi power; System power=153W; Tipologia=Bi power; Voltage-=220/240 V - 50/60 Hz - Bi-power with self-learning; Weight (kg)=8,4; Weight (kg):=8,4; Working temperature=-25 +40 °C
- GWR5675M30K - ROAD5 MEDI HUGE 5M 3000K 0,7A CL1 1-10V: Body=Die-cast aluminium -; Classification:=-; Color Rendering Index=CRI-70; Colore=Graphite grey; Colour :=Powder coating; Colour temperature=3000K; Colour temperature:=3000 K (CRI>80); Context=Street and parking lighting; Control System=Dimmable 1-10 V; DIN 18032-3 certification=-; Descrizione=GWR5675M30K - ROAD5 MEDI HUGE 5M 3000K 0,7A CL1 1-10V; Device with reduced surface temperature=-; Driver=Included; Driver Box=Built-in; Efficiency (lm/W)=97; Eletrical and lighting features=-; External screw=Stainless steel; Fixing=Pole Head - Outreach; Gasket=Anti-aging silicone; General information=-; Glow Wire Test :=-; IPEA=ROAD = B // LARGE AREAS = A ++ // CYCLOPEDONALS = A // GREEN AREAS = A // HISTORICAL CENTER = A3 +; Installationa and maintenance=-; LED Life Time (L80B05)=77000H; LED Maintenance=Not available; LED current.=0,7A; Lifetime=L90B10 (Tq+25°C) = 100.000 h - L90B10 (Tq+50°C) = 50.000 h; Locking Hook=Integrated front handle; Lumen output (lm)=13000; Luminaire=LED Road Equipment; Materials=-; Maximum surface exposed to the wind :=0.19 m2; Modello=GWR5675M30K; Mouting and installation=Pole Head - Outreach; Nominal flux (lm)=13500; Number of modules=5 (5x3 LED); Operating temperature :=-25 +50 °C; Operating temperature:=-25 +50 °C; Optic=HUGE; Optic :=Metallized polycarbonate reflector; Optic Maintenance=Not available; Optic and illuminating features=-; Overvoltage protection=DM 10KV / CM 10KV; Overvoltage resistance :=Common and dfferential mode: 10KV; Photobiological Risk Class=RG0; Power supply operation=Dimmable; Rated frequency (Hz)=50 / 60; Shield type=4mm thick flat tempered glass; Standard Deviation Colour Matching=SDCM = 5; Standard-=EN 60598-2-3, EN 60598-1 IEC/TR 62778; Standards and approvals=-; Stocking temperature=-; Supply voltage=220 - 240 V; System power=132W; System power :=134 W @ 0.7A; Tilt-=-20° ÷ +10° side bracket - -10° ÷ +20° pole head; Tipologia=Dimmable; Type of light source=LED - Not replaceable; Unified Glare Rating=G*3 - ULOR = 0; Unique digital code (Datamatrix)=Currently not present; Voltage-=220/240 V - 50/60 Hz - Dimmable 1-10 V; Weight (kg):=8,8; Wiring=Isolating switch
- GWR5615B - ROAD5 MEDI HUGE 5M 4000K 0,85A CL1 BIREG: Colour temperature=4000 K (CRI 70); Colour temperature:=4000 K (CRI 70); Descrizione=ROAD5 MEDI HUGE 5M 4000K 0,85A CL1 BI-PO; EAN code=8011564874367; LED LifeTime (L80B05)=120000H; LED current.=0,85A; Lumen output (lm)=14970; Modello=GWR5615B; No. Chorus modules=5 (5x3 LED); Nominal flux (lm)=21230; Number of modules=5 (5x3 LED); Operating temperature:=-25 +40 °C; Optic=H - ULOR: 0%; Overvoltage resistance=12 KV (Common and dfferential mode); Pilot current=0,85A; Power supply operation=Bi power; System power=161W; Tipologia=Bi power; Voltage-=220/240 V - 50/60 Hz - Bi-power with self-learning; Weight (kg)=8,8; Weight (kg):=8,8; Working temperature=-25 +40 °C
- GWR5616 - ROAD5 MEDI HUGE 6M 4000K 0,85A CL1: Colour temperature=4000 K (CRI 70); Colour temperature:=4000 K (CRI 70); Descrizione=ROAD5 MEDI HUGE 6M 4000K 0,85A CL1; EAN code=8011564874381; LED LifeTime (L80B05)=120000H; LED current.=0,85A; Lumen output (lm)=17162; Modello=GWR5616; No. Chorus modules=6 (6x3 LED); Nominal flux (lm)=24327; Number of modules=6 (6x3 LED); Operating temperature:=-25 +40 °C; Optic=H - ULOR: 0%; Overvoltage resistance=12 KV (Common and dfferential mode); Pilot current=0,85A; System power=185W; Tipologia=Stand alone; Voltage-=220/240 V - 50/60 Hz - Stand alone; Weight (kg)=9.1; Weight (kg):=9,1; Working temperature=-25 +40 °C
- GWR561430K - ROAD5 MEDI HUGE 4M 3000K 1,0A CL1: Body=Die-cast aluminium -; Classification:=-; Color Rendering Index=CRI-70; Colore=Graphite grey; Colour :=Powder coating; Colour temperature=3000K; Colour temperature:=3000 K (CRI>80); Context=Street and parking lighting; Control System=Stand alone; DIN 18032-3 certification=-; Descrizione=GWR561430K - ROAD5 MEDI HUGE 4M 3000K 1,0A CL1; Device with reduced surface temperature=-; Driver=Included; Driver Box=Built-in; Efficiency (lm/W)=93; Eletrical and lighting features=-; External screw=Stainless steel; Fixing=Pole Head - Outreach; Gasket=Anti-aging silicone; General information=-; Glow Wire Test :=-; IPEA=ROAD = B // LARGE AREAS = A + // CYCLOPEDONALS = B // GREEN AREAS = B // HISTORICAL CENTER = A3 +; Installationa and maintenance=-; LED Life Time (L80B05)=120000H; LED Maintenance=Not available; LED current.=1A; Lifetime=L90B10 (Tq+25°C) = 100.000 h - L90B10 (Tq+40°C) = 50.000 h; Locking Hook=Integrated front handle; Lumen output (lm)=14000; Luminaire=LED Road Equipment; Materials=-; Maximum surface exposed to the wind :=0.19 m2; Modello=GWR561430K; Mouting and installation=Pole Head - Outreach; Nominal flux (lm)=16560; Number of modules=4 (4x3 LED); Operating temperature :=-25 +40 °C; Operating temperature:=-25 +40 °C; Optic=HUGE; Optic :=Metallized polycarbonate reflector; Optic Maintenance=Not available; Optic and illuminating features=-; Overvoltage protection=DM 10KV / CM 10KV; Overvoltage resistance :=Common and dfferential mode: 10KV; Photobiological Risk Class=RG0; Rated frequency (Hz)=50 / 60; Shield type=4mm thick flat tempered glass; Standard Deviation Colour Matching=SDCM = 5; Standard-=EN 60598-2-3, EN 60598-1 IEC/TR 62778; Standards and approvals=-; Stocking temperature=-; Supply voltage=220 - 240 V; System power=151W; System power :=151 W @ 1A; Tilt-=-20° ÷ +10° side bracket - -10° ÷ +20° pole head; Tipologia=Stand alone; Type of light source=LED - Not replaceable; Unified Glare Rating=G*3 - ULOR = 0; Unique digital code (Datamatrix)=Currently not present; Voltage-=220/240 V - 50/60 Hz - Stand alone; Weight (kg):=8,4; Wiring=Isolating switch
- GWR5614B30K - ROAD5 MEDI HUGE 4M 3000K 1,0A CL1 BIREG: Body=Die-cast aluminium -; Classification:=-; Color Rendering Index=CRI-70; Colore=Graphite grey; Colour :=Powder coating; Colour temperature=3000K; Colour temperature:=3000 K (CRI>80); Context=Street and parking lighting; Control System=Bi-power with self-learning; DIN 18032-3 certification=-; Descrizione=GWR5614B30K - ROAD5 MEDI HUGE 4M 3000K 1,0A CL1 BIREG; Device with reduced surface temperature=-; Driver=Included; Driver Box=Built-in; Efficiency (lm/W)=92; Eletrical and lighting features=-; External screw=Stainless steel; Fixing=Pole Head - Outreach; Gasket=Anti-aging silicone; General information=-; Glow Wire Test :=-; IPEA=ROAD = B // LARGE AREAS = A + // CYCLOPEDONALS = B // GREEN AREAS = B // HISTORICAL CENTER = A3 +; Installationa and maintenance=-; LED Life Time (L80B05)=120000H; LED Maintenance=Not available; LED current.=1A; Lifetime=L90B10 (Tq+25°C) = 100.000 h - L90B10 (Tq+40°C) = 50.000 h; Locking Hook=Integrated front handle; Lumen output (lm)=14000; Luminaire=LED Road Equipment; Materials=-; Maximum surface exposed to the wind :=0.19 m2; Modello=GWR5614B30K; Mouting and installation=Pole Head - Outreach; Nominal flux (lm)=16560; Number of modules=4 (4x3 LED); Operating temperature :=-25 +40 °C; Operating temperature:=-25 +40 °C; Optic=HUGE; Optic :=Metallized polycarbonate reflector; Optic Maintenance=Not available; Optic and illuminating features=-; Overvoltage protection=DM 10KV / CM 10KV; Overvoltage resistance :=Common and dfferential mode: 10KV; Photobiological Risk Class=RG0; Power supply operation=Bi power; Rated frequency (Hz)=50 / 60; Shield type=4mm thick flat tempered glass; Standard Deviation Colour Matching=SDCM = 5; Standard-=EN 60598-2-3, EN 60598-1 IEC/TR 62778; Standards and approvals=-; Stocking temperature=-; Supply voltage=220 - 240 V; System power=153W; System power :=153 W @ 1A; Tilt-=-20° ÷ +10° side bracket - -10° ÷ +20° pole head; Tipologia=Bi power; Type of light source=LED - Not replaceable; Unified Glare Rating=G*3 - ULOR = 0; Unique digital code (Datamatrix)=Currently not present; Voltage-=220/240 V - 50/60 Hz - Bi-power with self-learning; Weight (kg):=8,4; Wiring=Isolating switch
- GWR5614M - ROAD5 MEDI HUGE 4M 4000K 1,0A CL1 1-10V: Colour temperature=4000 K (CRI 70); Colour temperature:=4000 K (CRI 70); Descrizione=ROAD5 MEDI HUGE 4M 4000K 1,0A CL1 1-10V; EAN code=8011564874343; LED LifeTime (L80B05)=120000H; LED current.=1A; Lumen output (lm)=13460; Modello=GWR5614M; No. Chorus modules=4 (4x3 LED); Nominal flux (lm)=19080; Number of modules=4 (4x3 LED); Operating temperature:=-25 +40 °C; Optic=H - ULOR: 0%; Overvoltage resistance=12 KV (Common and dfferential mode); Pilot current=1A; Power supply operation=Dimmable; System power=113W; Tipologia=Dimmable; Voltage-=220/240 V - 50/60 Hz - Dimmable 1-10 V; Weight (kg)=8,4; Weight (kg):=8,4; Working temperature=-25 +40 °C
- GWR5615 - ROAD5 MEDI HUGE 5M 4000K 0,85A CL1: Colour temperature=4000 K (CRI 70); Colour temperature:=4000 K (CRI 70); Descrizione=ROAD5 MEDI HUGE 5M 4000K 0,85A CL1; EAN code=8011564874350; LED LifeTime (L80B05)=120000H; LED current.=0,85A; Lumen output (lm)=14974; Modello=GWR5615; No. Chorus modules=5 (5x3 LED); Nominal flux (lm)=21227; Number of modules=5 (5x3 LED); Operating temperature:=-25 +40 °C; Optic=H - ULOR: 0%; Overvoltage resistance=12 KV (Common and dfferential mode); Pilot current=0,85A; System power=159W; Tipologia=Stand alone; Voltage-=220/240 V - 50/60 Hz - Stand alone; Weight (kg)=8,8; Weight (kg):=8,8; Working temperature=-25 +40 °C
- GWR5615M - ROAD5 MEDI HUGE 5M 4000K 0,85A CL1 1-10V: Colour temperature=4000 K (CRI 70); Colour temperature:=4000 K (CRI 70); Descrizione=ROAD5 MEDI HUGE 5M 4000K 0,85A CL1 1-10V; EAN code=8011564874374; LED LifeTime (L80B05)=120000H; LED current.=0,85A; Lumen output (lm)=14970; Modello=GWR5615M; No. Chorus modules=5 (5x3 LED); Nominal flux (lm)=21230; Number of modules=5 (5x3 LED); Operating temperature:=-25 +40 °C; Optic=H - ULOR: 0%; Overvoltage resistance=12 KV (Common and dfferential mode); Pilot current=0,85A; Power supply operation=Dimmable; System power=159W; Tipologia=Dimmable; Voltage-=220/240 V - 50/60 Hz - Dimmable 1-10 V; Weight (kg)=8,8; Weight (kg):=8,8; Working temperature=-25 +40 °C
- GWR561530K - ROAD5 MEDI HUGE 5M 3000K 0,85A CL1: Body=Die-cast aluminium -; Classification:=-; Color Rendering Index=CRI-70; Colore=Graphite grey; Colour :=Powder coating; Colour temperature=3000K; Colour temperature:=3000 K (CRI>80); Context=Street and parking lighting; Control System=Stand alone; DIN 18032-3 certification=-; Descrizione=GWR561530K - ROAD5 MEDI HUGE 5M 3000K 0,85A CL1; Device with reduced surface temperature=-; Driver=Included; Driver Box=Built-in; Efficiency (lm/W)=96; Eletrical and lighting features=-; External screw=Stainless steel; Fixing=Pole Head - Outreach; Gasket=Anti-aging silicone; General information=-; Glow Wire Test :=-; IPEA=ROAD = B // LARGE AREAS = A ++ // CYCLOPEDONALS = B // GREEN AREAS = B // HISTORICAL CENTER = A3 +; Installationa and maintenance=-; LED Life Time (L80B05)=120000H; LED Maintenance=Not available; LED current.=0,849999999999999A; Lifetime=L90B10 (Tq+25°C) = 100.000 h - L90B10 (Tq+40°C) = 50.000 h; Locking Hook=Integrated front handle; Lumen output (lm)=15300; Luminaire=LED Road Equipment; Materials=-; Maximum surface exposed to the wind :=0.19 m2; Modello=GWR561530K; Mouting and installation=Pole Head - Outreach; Nominal flux (lm)=18423; Number of modules=5 (5x3 LED); Operating temperature :=-25 +40 °C; Operating temperature:=-25 +40 °C; Optic=HUGE; Optic :=Metallized polycarbonate reflector; Optic Maintenance=Not available; Optic and illuminating features=-; Overvoltage protection=DM 10KV / CM 10KV; Overvoltage resistance :=Common and dfferential mode: 10KV; Photobiological Risk Class=RG0; Rated frequency (Hz)=50 / 60; Shield type=4mm thick flat tempered glass; Standard Deviation Colour Matching=SDCM = 5; Standard-=EN 60598-2-3, EN 60598-1 IEC/TR 62778; Standards and approvals=-; Stocking temperature=-; Supply voltage=220 - 240 V; System power=159W; System power :=159 W @ 0.85A; Tilt-=-20° ÷ +10° side bracket - -10° ÷ +20° pole head; Tipologia=Stand alone; Type of light source=LED - Not replaceable; Unified Glare Rating=G*3 - ULOR = 0; Unique digital code (Datamatrix)=Currently not present; Voltage-=220/240 V - 50/60 Hz - Stand alone; Weight (kg):=8,8; Wiring=Isolating switch
- GWR5675B - ROAD5 MEDI HUGE 5M 4000K 0,7A CL1 BIREG: Colour temperature=4000 K (CRI 70); Colour temperature:=4000 K (CRI 70); Descrizione=ROAD5 MEDI HUGE 5M 4000K 0,7A CL1 BI-POW; EAN code=8011564874558; LED LifeTime (L80B05)=77000H; LED current.=0,7A; Lumen output (lm)=11480; Modello=GWR5675B; No. Chorus modules=5 (5x3 LED); Nominal flux (lm)=15600; Number of modules=5 (5x3 LED); Operating temperature:=-25 +50 °C; Optic=H - ULOR: 0%; Overvoltage resistance=12 KV (Common and dfferential mode); Pilot current=0,7A; Power supply operation=Bi power; System power=134W; Tipologia=Bi power; Voltage-=220/240 V - 50/60 Hz - Bi-power with self-learning; Weight (kg)=8,8; Weight (kg):=8,8; Working temperature=-25 +50 °C
- GWR5613M30K - ROAD5 MEDI HUGE 3M 3000K 1,0A CL1 1-10V: Body=Die-cast aluminium -; Classification:=-; Color Rendering Index=CRI-70; Colore=Graphite grey; Colour :=Powder coating; Colour temperature=3000K; Colour temperature:=3000 K (CRI>80); Context=Street and parking lighting; Control System=Dimmable 1-10 V; DIN 18032-3 certification=-; Descrizione=GWR5613M30K - ROAD5 MEDI HUGE 3M 3000K 1,0A CL1 1-10V; Device with reduced surface temperature=-; Driver=Included; Driver Box=Built-in; Efficiency (lm/W)=91; Eletrical and lighting features=-; External screw=Stainless steel; Fixing=Pole Head - Outreach; Gasket=Anti-aging silicone; General information=-; Glow Wire Test :=-; IPEA=ROAD = A // LARGE AREAS = A ++ // CYCLOPEDONALS = B // GREEN AREAS = B // HISTORICAL CENTER = A3 +; Installationa and maintenance=-; LED Life Time (L80B05)=120000H; LED Maintenance=Not available; LED current.=1A; Lifetime=L90B10 (Tq+25°C) = 100.000 h - L90B10 (Tq+40°C) = 75.000 h; Locking Hook=Integrated front handle; Lumen output (lm)=10500; Luminaire=LED Road Equipment; Materials=-; Maximum surface exposed to the wind :=0.19 m2; Modello=GWR5613M30K; Mouting and installation=Pole Head - Outreach; Nominal flux (lm)=12420; Number of modules=3 (3x3 LED); Operating temperature :=-25 +40 °C; Operating temperature:=-25 +40 °C; Optic=HUGE; Optic :=Metallized polycarbonate reflector; Optic Maintenance=Not available; Optic and illuminating features=-; Overvoltage protection=DM 10KV / CM 10KV; Overvoltage resistance :=Common and dfferential mode: 10KV; Photobiological Risk Class=RG0; Power supply operation=Dimmable; Rated frequency (Hz)=50 / 60; Shield type=4mm thick flat tempered glass; Standard Deviation Colour Matching=SDCM = 5; Standard-=EN 60598-2-3, EN 60598-1 IEC/TR 62778; Standards and approvals=-; Stocking temperature=-; Supply voltage=220 - 240 V; System power=113W; System power :=115 W @ 1A; Tilt-=-20° ÷ +10° side bracket - -10° ÷ +20° pole head; Tipologia=Dimmable; Type of light source=LED - Not replaceable; Unified Glare Rating=G*3 - ULOR = 0; Unique digital code (Datamatrix)=Currently not present; Voltage-=220/240 V - 50/60 Hz - Dimmable 1-10 V; Weight (kg):=8; Wiring=Isolating switch
- GWR5614M30K - ROAD5 MEDI HUGE 4M 3000K 1,0A CL1 1-10V: Body=Die-cast aluminium -; Classification:=-; Color Rendering Index=CRI-70; Colore=Graphite grey; Colour :=Powder coating; Colour temperature=3000K; Colour temperature:=3000 K (CRI>80); Context=Street and parking lighting; Control System=Dimmable 1-10 V; DIN 18032-3 certification=-; Descrizione=GWR5614M30K - ROAD5 MEDI HUGE 4M 3000K 1,0A CL1 1-10V; Device with reduced surface temperature=-; Driver=Included; Driver Box=Built-in; Efficiency (lm/W)=92; Eletrical and lighting features=-; External screw=Stainless steel; Fixing=Pole Head - Outreach; Gasket=Anti-aging silicone; General information=-; Glow Wire Test :=-; IPEA=ROAD = B // LARGE AREAS = A + // CYCLOPEDONALS = B // GREEN AREAS = B // HISTORICAL CENTER = A3 +; Installationa and maintenance=-; LED Life Time (L80B05)=120000H; LED Maintenance=Not available; LED current.=1A; Lifetime=L90B10 (Tq+25°C) = 100.000 h - L90B10 (Tq+40°C) = 50.000 h; Locking Hook=Integrated front handle; Lumen output (lm)=14000; Luminaire=LED Road Equipment; Materials=-; Maximum surface exposed to the wind :=0.19 m2; Modello=GWR5614M30K; Mouting and installation=Pole Head - Outreach; Nominal flux (lm)=16560; Number of modules=4 (4x3 LED); Operating temperature :=-25 +40 °C; Operating temperature:=-25 +40 °C; Optic=HUGE; Optic :=Metallized polycarbonate reflector; Optic Maintenance=Not available; Optic and illuminating features=-; Overvoltage protection=DM 10KV / CM 10KV; Overvoltage resistance :=Common and dfferential mode: 10KV; Photobiological Risk Class=RG0; Power supply operation=Dimmable; Rated frequency (Hz)=50 / 60; Shield type=4mm thick flat tempered glass; Standard Deviation Colour Matching=SDCM = 5; Standard-=EN 60598-2-3, EN 60598-1 IEC/TR 62778; Standards and approvals=-; Stocking temperature=-; Supply voltage=220 - 240 V; System power=113W; System power :=153 W @ 1A; Tilt-=-20° ÷ +10° side bracket - -10° ÷ +20° pole head; Tipologia=Dimmable; Type of light source=LED - Not replaceable; Unified Glare Rating=G*3 - ULOR = 0; Unique digital code (Datamatrix)=Currently not present; Voltage-=220/240 V - 50/60 Hz - Dimmable 1-10 V; Weight (kg):=8,4; Wiring=Isolating switch

## geometry (parser evidence)
native form markers: Blend x2
no freeform markers — native parametric forms only
